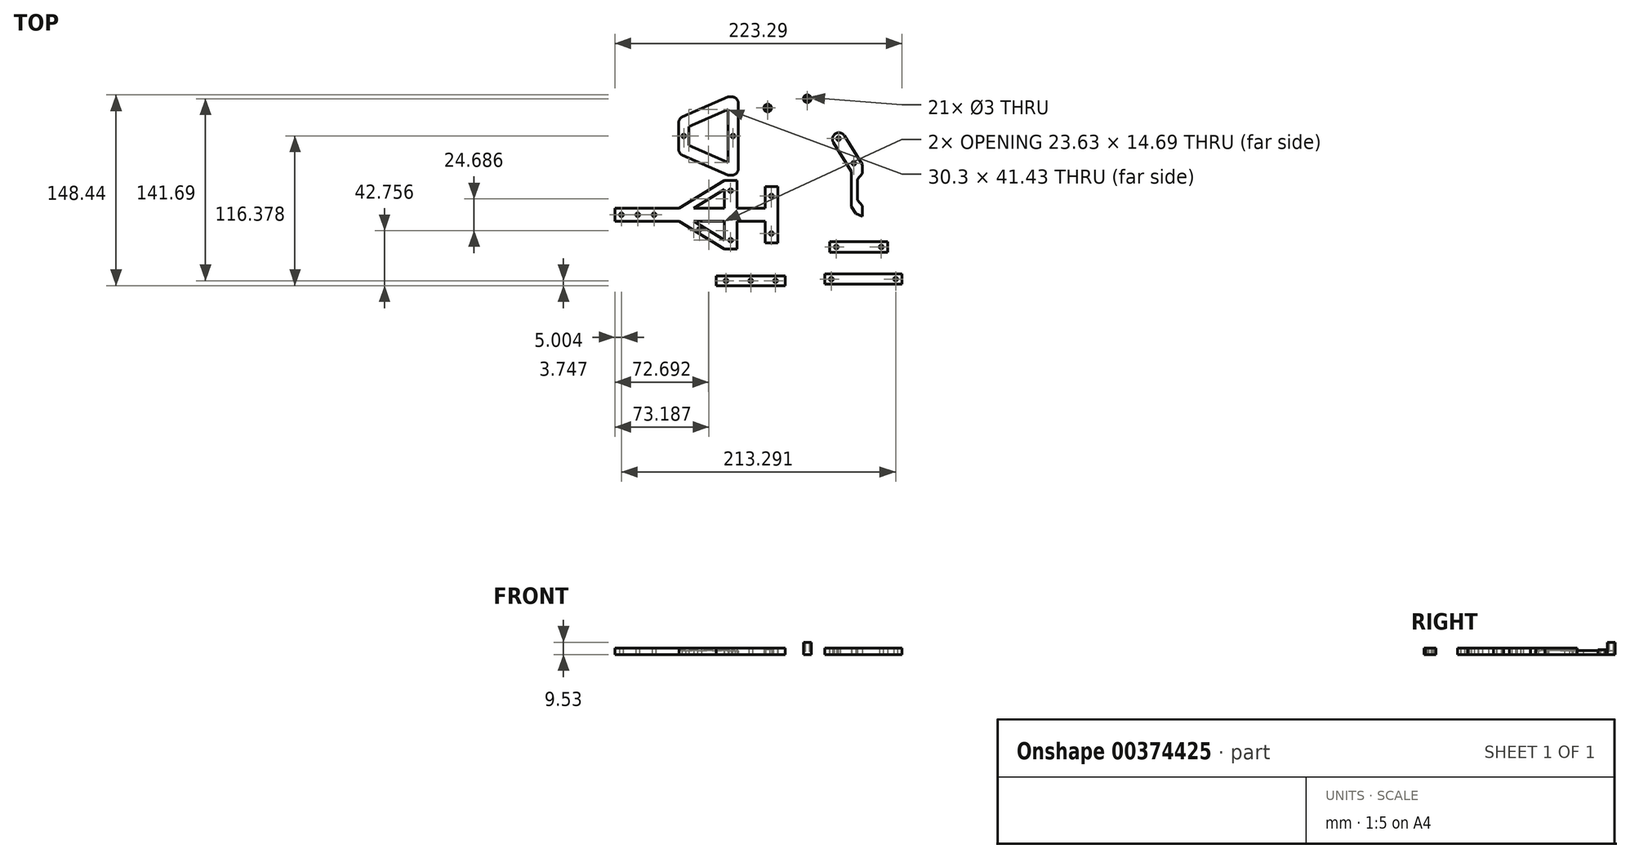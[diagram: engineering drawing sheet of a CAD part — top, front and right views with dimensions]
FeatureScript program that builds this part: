
annotation { "Feature Type Name" : "Feature", "Feature Type Description" : "" }
export const myFeature = defineFeature(function(context is Context, id is Id, definition is map)
    precondition{}
    {
        {
            var Q0;
            Q0=qCreatedBy(makeId("Top.planeOp"),FACE);
            var sketch = newSketch(context, id + "F0", { "sketchPlane" : qUnion([Q0])});
            skLineSegment(sketch, "E0.bottom", {"start": v(-43.53, 84.94) * mm, "end": v(-108.53, 84.94) * mm});
            skLineSegment(sketch, "E0.top", {"start": v(-43.53, 65.26) * mm, "end": v(-108.53, 65.26) * mm});
            skLineSegment(sketch, "E0.left", {"start": v(-43.53, 84.94) * mm, "end": v(-43.53, 65.26) * mm});
            skLineSegment(sketch, "E0.right", {"start": v(-108.53, 84.94) * mm, "end": v(-108.53, 65.26) * mm});
            skPoint(sketch, "E0.middle", {"position": v(-76.03, 75.1) * mm});
            skCircle(sketch, "E1", {"center": v(-96.03, 75.1) * mm, "radius": 1.5 * mm});
            skCircle(sketch, "E2", {"center": v(-57.73, 75.1) * mm, "radius": 1.5 * mm});
            skLineSegment(sketch, "E3.bottom", {"start": v(-49.57, 18.82) * mm, "end": v(-149.57, 18.82) * mm});
            skLineSegment(sketch, "E3.top", {"start": v(-49.57, 8.82) * mm, "end": v(-149.57, 8.82) * mm});
            skLineSegment(sketch, "E3.left", {"start": v(-49.57, 18.82) * mm, "end": v(-49.57, 8.82) * mm});
            skLineSegment(sketch, "E3.right", {"start": v(-149.57, 18.82) * mm, "end": v(-149.57, 8.82) * mm});
            skPoint(sketch, "E3.middle", {"position": v(-99.57, 13.82) * mm});
            skCircle(sketch, "E4", {"center": v(-144.57, 13.82) * mm, "radius": 1.5 * mm});
            skCircle(sketch, "E5", {"center": v(-119.17, 13.82) * mm, "radius": 1.5 * mm});
            skCircle(sketch, "E6", {"center": v(-131.87, 13.82) * mm, "radius": 1.5 * mm});
            skLineSegment(sketch, "E7.bottom", {"start": v(-53.73, 95.81) * mm, "end": v(-61.73, 95.81) * mm});
            skLineSegment(sketch, "E7.top", {"start": v(-53.73, 54.38) * mm, "end": v(-61.73, 54.38) * mm});
            skLineSegment(sketch, "E7.left", {"start": v(-53.73, 95.81) * mm, "end": v(-53.73, 54.38) * mm});
            skLineSegment(sketch, "E7.right", {"start": v(-61.73, 95.81) * mm, "end": v(-61.73, 54.38) * mm});
            skLineSegment(sketch, "E8", {"start": v(-61.73, 95.81) * mm, "end": v(-108.53, 75.1) * mm});
            skLineSegment(sketch, "E9", {"start": v(-108.53, 75.1) * mm, "end": v(-61.73, 54.38) * mm});
            skLineSegment(sketch, "E10", {"start": v(-108.53, 84.94) * mm, "end": v(-61.73, 105.66) * mm});
            skLineSegment(sketch, "E11", {"start": v(-61.73, 105.66) * mm, "end": v(-53.73, 105.66) * mm});
            skLineSegment(sketch, "E12", {"start": v(-53.73, 105.66) * mm, "end": v(-53.73, 95.81) * mm});
            skLineSegment(sketch, "E13", {"start": v(-108.53, 65.26) * mm, "end": v(-61.73, 44.54) * mm});
            skLineSegment(sketch, "E14", {"start": v(-61.73, 44.54) * mm, "end": v(-53.73, 44.54) * mm});
            skLineSegment(sketch, "E15", {"start": v(-53.73, 44.54) * mm, "end": v(-53.73, 54.38) * mm});
            skLineSegment(sketch, "E16", {"start": v(-100.03, 61.5) * mm, "end": v(-100.03, 88.7) * mm});
            skLineSegment(sketch, "E17", {"start": v(-92.03, 57.95) * mm, "end": v(-92.03, 92.24) * mm});
            skCircle(sketch, "E18", {"center": v(-30.8, 96.92) * mm, "radius": 1.5 * mm});
            skCircle(sketch, "E19", {"center": v(-30.8, 96.92) * mm, "radius": 3 * mm});
            skCircle(sketch, "E20", {"center": v(24.35, 73.1) * mm, "radius": 1.5 * mm});
            skLineSegment(sketch, "E21", {"start": v(24.35, 73.1) * mm, "end": v(24.35, 53.98) * mm, "construction": true});
            skLineSegment(sketch, "E22", {"start": v(24.35, 53.98) * mm, "end": v(36.2, 53.98) * mm, "construction": true});
            skLineSegment(sketch, "E23", {"start": v(36.2, 53.98) * mm, "end": v(24.35, 73.1) * mm, "construction": true});
            skCircle(sketch, "E24", {"center": v(36.2, 53.98) * mm, "radius": 1.5 * mm});
            skLineSegment(sketch, "E25", {"start": v(24.35, 73.1) * mm, "end": v(20.1, 70.47) * mm});
            skLineSegment(sketch, "E26", {"start": v(20.1, 70.47) * mm, "end": v(31.95, 51.34) * mm});
            skLineSegment(sketch, "E27", {"start": v(20.1, 70.47) * mm, "end": v(17.73, 74.3) * mm});
            skLineSegment(sketch, "E28", {"start": v(17.73, 74.3) * mm, "end": v(21.98, 76.93) * mm});
            skLineSegment(sketch, "E29", {"start": v(21.98, 76.93) * mm, "end": v(24.35, 73.1) * mm});
            skLineSegment(sketch, "E30", {"start": v(30.27, 63.54) * mm, "end": v(26.02, 60.9) * mm});
            skLineSegment(sketch, "E31.MirrorCS", {"start": v(28.6, 75.74) * mm, "end": v(40.45, 56.6) * mm});
            skLineSegment(sketch, "E32.MirrorCS", {"start": v(28.6, 75.74) * mm, "end": v(26.23, 79.56) * mm});
            skLineSegment(sketch, "E33.MirrorCS", {"start": v(26.23, 79.56) * mm, "end": v(21.98, 76.93) * mm});
            skLineSegment(sketch, "E34.MirrorCS", {"start": v(34.32, 47.52) * mm, "end": v(38.57, 50.15) * mm});
            skLineSegment(sketch, "E35.MirrorCS", {"start": v(42.82, 52.78) * mm, "end": v(38.57, 50.15) * mm});
            skLineSegment(sketch, "E36.MirrorCS", {"start": v(40.45, 56.6) * mm, "end": v(42.82, 52.78) * mm});
            skLineSegment(sketch, "E37", {"start": v(31.95, 51.34) * mm, "end": v(34.32, 47.52) * mm});
            skPoint(sketch, "E38.endSnap0", {"position": v(40.7, 51.47) * mm});
            skLineSegment(sketch, "E39", {"start": v(42.82, 52.78) * mm, "end": v(42.82, 45.78) * mm});
            skLineSegment(sketch, "E40", {"start": v(42.82, 45.78) * mm, "end": v(38.9, 45.78) * mm});
            skLineSegment(sketch, "E41", {"start": v(38.9, 45.78) * mm, "end": v(38.9, 20.78) * mm});
            skLineSegment(sketch, "E42", {"start": v(38.9, 20.78) * mm, "end": v(42.82, 20.78) * mm});
            skLineSegment(sketch, "E43", {"start": v(42.82, 20.78) * mm, "end": v(42.82, 12.66) * mm});
            skLineSegment(sketch, "E44", {"start": v(34.32, 47.52) * mm, "end": v(34.32, 20.16) * mm});
            skLineSegment(sketch, "E45", {"start": v(34.32, 20.16) * mm, "end": v(37.65, 14.77) * mm});
            skLineSegment(sketch, "E46", {"start": v(37.65, 14.77) * mm, "end": v(42.82, 12.66) * mm});
            skLineSegment(sketch, "E47", {"start": v(38.9, 33.28) * mm, "end": v(34.32, 33.28) * mm});
            skPoint(sketch, "E47.endSnap0", {"position": v(34.32, 33.84) * mm});
            skLineSegment(sketch, "E48", {"start": v(42.82, 45.78) * mm, "end": v(38.9, 41.43) * mm});
            skLineSegment(sketch, "E49.MirrorCS", {"start": v(42.82, 20.78) * mm, "end": v(38.9, 25.13) * mm});
            skCircle(sketch, "E50", {"center": v(-63.23, -37.53) * mm, "radius": 1.5 * mm});
            skCircle(sketch, "E51", {"center": v(-24.73, -37.53) * mm, "radius": 1.5 * mm});
            skLineSegment(sketch, "E52", {"start": v(-63.23, -37.53) * mm, "end": v(-24.73, -37.53) * mm});
            skLineSegment(sketch, "E53.bottom", {"start": v(-17.23, -33.78) * mm, "end": v(-70.73, -33.78) * mm});
            skLineSegment(sketch, "E53.top", {"start": v(-17.23, -41.28) * mm, "end": v(-70.73, -41.28) * mm});
            skLineSegment(sketch, "E53.left", {"start": v(-17.23, -33.78) * mm, "end": v(-17.23, -41.28) * mm});
            skLineSegment(sketch, "E53.right", {"start": v(-70.73, -33.78) * mm, "end": v(-70.73, -41.28) * mm});
            skPoint(sketch, "E53.middle", {"position": v(-43.98, -37.53) * mm});
            skPoint(sketch, "E54.centerSnap0", {"position": v(-49.57, 13.82) * mm});
            skCircle(sketch, "E55", {"center": v(-43.98, -37.53) * mm, "radius": 1.5 * mm});
            skCircle(sketch, "E56", {"center": v(-59.57, 32.57) * mm, "radius": 1.5 * mm});
            skLineSegment(sketch, "E57", {"start": v(-59.57, 32.57) * mm, "end": v(-59.57, -5.93) * mm});
            skCircle(sketch, "E58", {"center": v(-59.57, -5.93) * mm, "radius": 1.5 * mm});
            skLineSegment(sketch, "E59.bottom", {"start": v(-54.57, 40.57) * mm, "end": v(-64.57, 40.57) * mm});
            skLineSegment(sketch, "E59.top", {"start": v(-54.57, -12.93) * mm, "end": v(-64.57, -12.93) * mm});
            skLineSegment(sketch, "E59.left", {"start": v(-54.57, 40.57) * mm, "end": v(-54.57, -12.93) * mm});
            skLineSegment(sketch, "E59.right", {"start": v(-64.57, 40.57) * mm, "end": v(-64.57, -12.93) * mm});
            skPoint(sketch, "E59.middle", {"position": v(-59.57, 13.82) * mm});
            skLineSegment(sketch, "E60", {"start": v(-64.57, 40.57) * mm, "end": v(-99.57, 18.82) * mm});
            skLineSegment(sketch, "E61", {"start": v(-88.2, 18.82) * mm, "end": v(-64.57, 33.5) * mm});
            skLineSegment(sketch, "E62", {"start": v(-49.57, 18.82) * mm, "end": v(-27.86, 18.82) * mm});
            skLineSegment(sketch, "E63", {"start": v(-27.86, 18.82) * mm, "end": v(-27.86, 8.82) * mm});
            skLineSegment(sketch, "E64", {"start": v(-27.86, 8.82) * mm, "end": v(-49.57, 8.82) * mm});
            skLineSegment(sketch, "E65.bottom", {"start": v(-22.86, 35.82) * mm, "end": v(-32.86, 35.82) * mm});
            skLineSegment(sketch, "E65.top", {"start": v(-22.86, -8.19) * mm, "end": v(-32.86, -8.19) * mm});
            skLineSegment(sketch, "E65.left", {"start": v(-22.86, 35.82) * mm, "end": v(-22.86, -8.19) * mm});
            skLineSegment(sketch, "E65.right", {"start": v(-32.86, 35.82) * mm, "end": v(-32.86, -8.19) * mm});
            skPoint(sketch, "E65.middle", {"position": v(-27.86, 13.82) * mm});
            skCircle(sketch, "E66", {"center": v(-27.86, 28.42) * mm, "radius": 1.5 * mm});
            skPoint(sketch, "E66.centerSnap0", {"position": v(-27.86, 35.82) * mm});
            skLineSegment(sketch, "E67", {"start": v(-64.57, 13.82) * mm, "end": v(-54.57, 13.82) * mm});
            skCircle(sketch, "E68.MirrorC", {"center": v(-27.86, -0.78) * mm, "radius": 1.5 * mm});
            skCircle(sketch, "E69", {"center": v(0, 104.16) * mm, "radius": 1.5 * mm});
            skCircle(sketch, "E70", {"center": v(0, 104.16) * mm, "radius": 3 * mm});
            skLineSegment(sketch, "E71.bottom", {"start": v(73.72, -32.22) * mm, "end": v(13.72, -32.22) * mm});
            skLineSegment(sketch, "E71.top", {"start": v(73.72, -40.22) * mm, "end": v(13.72, -40.22) * mm});
            skLineSegment(sketch, "E71.left", {"start": v(73.72, -32.22) * mm, "end": v(73.72, -40.22) * mm});
            skLineSegment(sketch, "E71.right", {"start": v(13.72, -32.22) * mm, "end": v(13.72, -40.22) * mm});
            skPoint(sketch, "E71.middle", {"position": v(43.72, -36.22) * mm});
            skLineSegment(sketch, "E72.bottom", {"start": v(62.58, -7.2) * mm, "end": v(17.58, -7.2) * mm});
            skLineSegment(sketch, "E72.top", {"start": v(62.58, -15.2) * mm, "end": v(17.58, -15.2) * mm});
            skLineSegment(sketch, "E72.left", {"start": v(62.58, -7.2) * mm, "end": v(62.58, -15.2) * mm});
            skLineSegment(sketch, "E72.right", {"start": v(17.58, -7.2) * mm, "end": v(17.58, -15.2) * mm});
            skPoint(sketch, "E72.middle", {"position": v(40.08, -11.2) * mm});
            skCircle(sketch, "E73", {"center": v(22.58, -11.2) * mm, "radius": 1.5 * mm});
            skLineSegment(sketch, "E74", {"start": v(40.08, -15.2) * mm, "end": v(40.08, -7.2) * mm});
            skLineSegment(sketch, "E75", {"start": v(43.72, -40.22) * mm, "end": v(43.72, -32.22) * mm});
            skCircle(sketch, "E76.MirrorC", {"center": v(57.58, -11.2) * mm, "radius": 1.5 * mm});
            skCircle(sketch, "E77", {"center": v(18.72, -36.22) * mm, "radius": 1.5 * mm});
            skPoint(sketch, "E77.centerSnap0", {"position": v(13.72, -36.22) * mm});
            skCircle(sketch, "E78.MirrorC", {"center": v(68.72, -36.22) * mm, "radius": 1.5 * mm});
            skPoint(sketch, "E79.endSnap0", {"position": v(-99.57, 8.82) * mm});
            skLineSegment(sketch, "E80", {"start": v(-99.57, 8.82) * mm, "end": v(-64.57, -12.93) * mm});
            skLineSegment(sketch, "E81", {"start": v(-88.2, 8.82) * mm, "end": v(-64.57, -5.87) * mm});
            skLineSegment(sketch, "E82", {"start": v(-85.38, 0) * mm, "end": v(-82.2, 5.1) * mm});
            skCircle(sketch, "E83", {"center": v(-83.8, 2.55) * mm, "radius": 1.5 * mm});
            skSolve(sketch);
        }
        {
            var Q0;
            Q0=makeQuery(id+"F0.imprint","IMPRINT",FACE,{"disambiguationData":[TD([[makeQuery(id+"F0.imprint","IMPRINT",EDGE,{"derivedFrom":sQuery(id+"F0.wireOp",EDGE,"E0.bottom")}),1.0]])]});
            var Q1;
            {var subQ5=sQuery(id+"F0.wireOp",EDGE,"E7.top");Q1=makeQuery(id+"F0.imprint","IMPRINT",FACE,{"disambiguationData":[TD([[makeQuery(id+"F0.imprint","IMPRINT",EDGE,{"derivedFrom":subQ5}),-1.0]])]});}
            var Q2;
            Q2=makeQuery(id+"F0.imprint","IMPRINT",FACE,{"disambiguationData":[TD([[makeQuery(id+"F0.imprint","IMPRINT",EDGE,{"derivedFrom":sQuery(id+"F0.wireOp",EDGE,"E2")}),-1.0]])]});
            var Q3;
            {var subQ4=sQuery(id+"F0.wireOp",EDGE,"E7.top");Q3=makeQuery(id+"F0.imprint","IMPRINT",FACE,{"disambiguationData":[TD([[makeQuery(id+"F0.imprint","IMPRINT",EDGE,{"derivedFrom":subQ4}),1.0]])]});}
            var Q4;
            {var subQ5=sQuery(id+"F0.wireOp",EDGE,"E9");var subQ6=sQuery(id+"F0.wireOp",EDGE,"E0.top");var subQ7=makeQuery(id+"F0.imprint","INTERSECT",VERTEX,{"derivedFrom":[subQ6,subQ5]});Q4=makeQuery(id+"F0.imprint","IMPRINT",FACE,{"disambiguationData":[TD([[makeQuery(id+"F0.imprint","IMPRINT",EDGE,{"disambiguationData":[TD([[subQ7,-1.0]])],"derivedFrom":subQ6}),1.0]])]});}
            var Q5;
            {var subQ0=sQuery(id+"F0.wireOp",EDGE,"E17");var subQ1=sQuery(id+"F0.wireOp",EDGE,"E0.top");var subQ2=makeQuery(id+"F0.imprint","INTERSECT",VERTEX,{"derivedFrom":[subQ1,subQ0]});Q5=makeQuery(id+"F0.imprint","IMPRINT",FACE,{"disambiguationData":[TD([[makeQuery(id+"F0.imprint","IMPRINT",EDGE,{"disambiguationData":[TD([[subQ2,-1.0]])],"derivedFrom":subQ1}),1.0]])]});}
            var Q6;
            {var subQ0=sQuery(id+"F0.wireOp",EDGE,"E9");var subQ1=sQuery(id+"F0.wireOp",EDGE,"E0.top");var subQ2=makeQuery(id+"F0.imprint","INTERSECT",VERTEX,{"derivedFrom":[subQ1,subQ0]});Q6=makeQuery(id+"F0.imprint","IMPRINT",FACE,{"disambiguationData":[TD([[makeQuery(id+"F0.imprint","IMPRINT",EDGE,{"disambiguationData":[TD([[subQ2,-1.0]])],"derivedFrom":subQ1}),-1.0]])]});}
            var Q7;
            Q7=makeQuery(id+"F0.imprint","IMPRINT",FACE,{"disambiguationData":[TD([[makeQuery(id+"F0.imprint","IMPRINT",EDGE,{"derivedFrom":sQuery(id+"F0.wireOp",EDGE,"E1")}),-1.0]])]});
            var Q8;
            {var subQ0=sQuery(id+"F0.wireOp",EDGE,"E17");var subQ1=sQuery(id+"F0.wireOp",EDGE,"E0.top");var subQ2=makeQuery(id+"F0.imprint","INTERSECT",VERTEX,{"derivedFrom":[subQ1,subQ0]});Q8=makeQuery(id+"F0.imprint","IMPRINT",FACE,{"disambiguationData":[TD([[makeQuery(id+"F0.imprint","IMPRINT",EDGE,{"disambiguationData":[TD([[subQ2,-1.0]])],"derivedFrom":subQ1}),-1.0]])]});}
            var Q9;
            {var subQ0=sQuery(id+"F0.wireOp",EDGE,"E17");var subQ1=sQuery(id+"F0.wireOp",EDGE,"E0.bottom");var subQ2=makeQuery(id+"F0.imprint","INTERSECT",VERTEX,{"derivedFrom":[subQ1,subQ0]});Q9=makeQuery(id+"F0.imprint","IMPRINT",FACE,{"disambiguationData":[TD([[makeQuery(id+"F0.imprint","IMPRINT",EDGE,{"disambiguationData":[TD([[subQ2,-1.0]])],"derivedFrom":subQ1}),1.0]])]});}
            var Q10;
            {var subQ0=sQuery(id+"F0.wireOp",EDGE,"E17");var subQ1=sQuery(id+"F0.wireOp",EDGE,"E0.bottom");var subQ2=makeQuery(id+"F0.imprint","INTERSECT",VERTEX,{"derivedFrom":[subQ1,subQ0]});Q10=makeQuery(id+"F0.imprint","IMPRINT",FACE,{"disambiguationData":[TD([[makeQuery(id+"F0.imprint","IMPRINT",EDGE,{"disambiguationData":[TD([[subQ2,-1.0]])],"derivedFrom":subQ1}),-1.0]])]});}
            var Q11;
            {var subQ5=sQuery(id+"F0.wireOp",EDGE,"E7.bottom");Q11=makeQuery(id+"F0.imprint","IMPRINT",FACE,{"disambiguationData":[TD([[makeQuery(id+"F0.imprint","IMPRINT",EDGE,{"derivedFrom":subQ5}),-1.0]])]});}
            var Q12;
            {var subQ5=sQuery(id+"F0.wireOp",EDGE,"E7.bottom");Q12=makeQuery(id+"F0.imprint","IMPRINT",FACE,{"disambiguationData":[TD([[makeQuery(id+"F0.imprint","IMPRINT",EDGE,{"derivedFrom":subQ5}),1.0]])]});}
            extrude(context, id + "F1", {"entities" : qUnion([Q0, Q1, Q2, Q3, Q4, Q5, Q6, Q7, Q8, Q9, Q10, Q11, Q12]), "depth" : 3.18 * mm});
        }
        {
            var Q0;
            Q0=makeQuery(id+"F0.imprint","IMPRINT",FACE,{"disambiguationData":[TD([[makeQuery(id+"F0.imprint","IMPRINT",EDGE,{"derivedFrom":sQuery(id+"F0.wireOp",EDGE,"E18")}),-1.0]])]});
            extrude(context, id + "F2", {"entities" : qUnion([Q0]), "depth" : 3.76 * mm});
        }
        {
            var Q0;
            Q0=makeQuery(id+"F0.imprint","IMPRINT",FACE,{"disambiguationData":[TD([[makeQuery(id+"F0.imprint","IMPRINT",EDGE,{"derivedFrom":sQuery(id+"F0.wireOp",EDGE,"E24")}),-1.0]])]});
            var Q1;
            {var subQ1=sQuery(id+"F0.wireOp",EDGE,"E27");Q1=makeQuery(id+"F0.imprint","IMPRINT",FACE,{"disambiguationData":[TD([[makeQuery(id+"F0.imprint","IMPRINT",EDGE,{"derivedFrom":subQ1}),-1.0]])]});}
            var Q2;
            {var subQ1=sQuery(id+"F0.wireOp",EDGE,"E34.MirrorCS");Q2=makeQuery(id+"F0.imprint","IMPRINT",FACE,{"disambiguationData":[TD([[makeQuery(id+"F0.imprint","IMPRINT",EDGE,{"derivedFrom":subQ1}),-1.0]])]});}
            var Q3;
            {var subQ0=sQuery(id+"F0.wireOp",EDGE,"E40");Q3=makeQuery(id+"F0.imprint","IMPRINT",FACE,{"disambiguationData":[TD([[makeQuery(id+"F0.imprint","IMPRINT",EDGE,{"derivedFrom":subQ0}),1.0]])]});}
            var Q4;
            {var subQ0=sQuery(id+"F0.wireOp",EDGE,"E42");Q4=makeQuery(id+"F0.imprint","IMPRINT",FACE,{"disambiguationData":[TD([[makeQuery(id+"F0.imprint","IMPRINT",EDGE,{"derivedFrom":subQ0}),-1.0]])]});}
            var Q5;
            {var subQ0=sQuery(id+"F0.wireOp",EDGE,"E42");Q5=makeQuery(id+"F0.imprint","IMPRINT",FACE,{"disambiguationData":[TD([[makeQuery(id+"F0.imprint","IMPRINT",EDGE,{"derivedFrom":subQ0}),1.0]])]});}
            var Q6;
            Q6=makeQuery(id+"F0.imprint","IMPRINT",FACE,{"disambiguationData":[TD([[makeQuery(id+"F0.imprint","IMPRINT",EDGE,{"derivedFrom":sQuery(id+"F0.wireOp",EDGE,"E50")}),-1.0]])]});
            var Q7;
            {var subQ0=sQuery(id+"F0.wireOp",EDGE,"E60");Q7=makeQuery(id+"F0.imprint","IMPRINT",FACE,{"disambiguationData":[TD([[makeQuery(id+"F0.imprint","IMPRINT",EDGE,{"derivedFrom":subQ0}),1.0]])]});}
            var Q8;
            Q8=makeQuery(id+"F0.imprint","IMPRINT",FACE,{"disambiguationData":[TD([[makeQuery(id+"F0.imprint","IMPRINT",EDGE,{"derivedFrom":sQuery(id+"F0.wireOp",EDGE,"E56")}),-1.0]])]});
            var Q9;
            {var subQ0=sQuery(id+"F0.wireOp",EDGE,"E57");var subQ1=sQuery(id+"F0.wireOp",EDGE,"E3.bottom");var subQ2=makeQuery(id+"F0.imprint","INTERSECT",VERTEX,{"derivedFrom":[subQ1,subQ0]});Q9=makeQuery(id+"F0.imprint","IMPRINT",FACE,{"disambiguationData":[TD([[makeQuery(id+"F0.imprint","IMPRINT",EDGE,{"disambiguationData":[TD([[subQ2,-1.0]])],"derivedFrom":subQ1}),1.0]])]});}
            var Q10;
            {var subQ0=sQuery(id+"F0.wireOp",EDGE,"E59.left");var subQ1=sQuery(id+"F0.wireOp",EDGE,"E3.bottom");var subQ2=makeQuery(id+"F0.imprint","INTERSECT",VERTEX,{"derivedFrom":[subQ1,subQ0]});Q10=makeQuery(id+"F0.imprint","IMPRINT",FACE,{"disambiguationData":[TD([[makeQuery(id+"F0.imprint","IMPRINT",EDGE,{"disambiguationData":[TD([[subQ2,-1.0]])],"derivedFrom":subQ1}),1.0]])]});}
            var Q11;
            Q11=makeQuery(id+"F0.imprint","IMPRINT",FACE,{"disambiguationData":[TD([[makeQuery(id+"F0.imprint","IMPRINT",EDGE,{"derivedFrom":sQuery(id+"F0.wireOp",EDGE,"E58")}),-1.0]])]});
            var Q12;
            {var subQ0=sQuery(id+"F0.wireOp",EDGE,"mOfxTBTb-6OkJ-vJrD-ISbf-gXZsoh9kn1xD");Q12=makeQuery(id+"F0.imprint","IMPRINT",FACE,{"disambiguationData":[TD([[makeQuery(id+"F0.imprint","IMPRINT",EDGE,{"derivedFrom":subQ0}),1.0]])]});}
            var Q13;
            {var subQ0=sQuery(id+"F0.wireOp",EDGE,"E3.right");Q13=makeQuery(id+"F0.imprint","IMPRINT",FACE,{"disambiguationData":[TD([[makeQuery(id+"F0.imprint","IMPRINT",EDGE,{"derivedFrom":subQ0}),1.0]])]});}
            var Q14;
            {var subQ0=sQuery(id+"F0.wireOp",EDGE,"E59.left");var subQ1=sQuery(id+"F0.wireOp",EDGE,"E3.top");var subQ2=makeQuery(id+"F0.imprint","INTERSECT",VERTEX,{"derivedFrom":[subQ1,subQ0]});Q14=makeQuery(id+"F0.imprint","IMPRINT",FACE,{"disambiguationData":[TD([[makeQuery(id+"F0.imprint","IMPRINT",EDGE,{"disambiguationData":[TD([[subQ2,-1.0]])],"derivedFrom":subQ1}),-1.0]])]});}
            var Q15;
            {var subQ0=sQuery(id+"F0.wireOp",EDGE,"E57");var subQ1=sQuery(id+"F0.wireOp",EDGE,"E3.top");var subQ2=makeQuery(id+"F0.imprint","INTERSECT",VERTEX,{"derivedFrom":[subQ1,subQ0]});Q15=makeQuery(id+"F0.imprint","IMPRINT",FACE,{"disambiguationData":[TD([[makeQuery(id+"F0.imprint","IMPRINT",EDGE,{"disambiguationData":[TD([[subQ2,-1.0]])],"derivedFrom":subQ1}),-1.0]])]});}
            var Q16;
            {var subQ4=sQuery(id+"F0.wireOp",EDGE,"E3.left");Q16=makeQuery(id+"F0.imprint","IMPRINT",FACE,{"disambiguationData":[TD([[makeQuery(id+"F0.imprint","IMPRINT",EDGE,{"derivedFrom":subQ4}),-1.0]])]});}
            var Q17;
            {var subQ0=sQuery(id+"F0.wireOp",EDGE,"E3.left");Q17=makeQuery(id+"F0.imprint","IMPRINT",FACE,{"disambiguationData":[TD([[makeQuery(id+"F0.imprint","IMPRINT",EDGE,{"derivedFrom":subQ0}),1.0]])]});}
            var Q18;
            {var subQ2=sQuery(id+"F0.wireOp",EDGE,"E63");Q18=makeQuery(id+"F0.imprint","IMPRINT",FACE,{"disambiguationData":[TD([[makeQuery(id+"F0.imprint","IMPRINT",EDGE,{"derivedFrom":subQ2}),1.0]])]});}
            var Q19;
            {var subQ0=sQuery(id+"F0.wireOp",EDGE,"E63");Q19=makeQuery(id+"F0.imprint","IMPRINT",FACE,{"disambiguationData":[TD([[makeQuery(id+"F0.imprint","IMPRINT",EDGE,{"derivedFrom":subQ0}),-1.0]])]});}
            var Q20;
            {var subQ0=sQuery(id+"F0.wireOp",EDGE,"E72.right");Q20=makeQuery(id+"F0.imprint","IMPRINT",FACE,{"disambiguationData":[TD([[makeQuery(id+"F0.imprint","IMPRINT",EDGE,{"derivedFrom":subQ0}),1.0]])]});}
            var Q21;
            {var subQ0=sQuery(id+"F0.wireOp",EDGE,"E72.left");Q21=makeQuery(id+"F0.imprint","IMPRINT",FACE,{"disambiguationData":[TD([[makeQuery(id+"F0.imprint","IMPRINT",EDGE,{"derivedFrom":subQ0}),-1.0]])]});}
            var Q22;
            {var subQ1=sQuery(id+"F0.wireOp",EDGE,"E71.left");Q22=makeQuery(id+"F0.imprint","IMPRINT",FACE,{"disambiguationData":[TD([[makeQuery(id+"F0.imprint","IMPRINT",EDGE,{"derivedFrom":subQ1}),-1.0]])]});}
            var Q23;
            {var subQ1=sQuery(id+"F0.wireOp",EDGE,"E71.right");Q23=makeQuery(id+"F0.imprint","IMPRINT",FACE,{"disambiguationData":[TD([[makeQuery(id+"F0.imprint","IMPRINT",EDGE,{"derivedFrom":subQ1}),1.0]])]});}
            var Q24;
            {var subQ1=sQuery(id+"F0.wireOp",EDGE,"xufnJeBo-MPzs-RzrS-7tlF-2dog0HHq910d");Q24=makeQuery(id+"F0.imprint","IMPRINT",FACE,{"disambiguationData":[TD([[makeQuery(id+"F0.imprint","IMPRINT",EDGE,{"derivedFrom":subQ1}),1.0]])]});}
            var Q25;
            {var subQ0=sQuery(id+"F0.wireOp",EDGE,"7ee9f3b0-d933-47a8-aa5e-a2f9af07bda80.MirrorCS");Q25=makeQuery(id+"F0.imprint","IMPRINT",FACE,{"disambiguationData":[TD([[makeQuery(id+"F0.imprint","IMPRINT",EDGE,{"derivedFrom":subQ0}),-1.0]])]});}
            var Q26;
            {var subQ4=sQuery(id+"F0.wireOp",EDGE,"7OHdfdEe-NtJ8-Z7NY-3w09-MJT2khb5SlhV");Q26=makeQuery(id+"F0.imprint","IMPRINT",FACE,{"disambiguationData":[TD([[makeQuery(id+"F0.imprint","IMPRINT",EDGE,{"derivedFrom":subQ4}),1.0]])]});}
            var Q27;
            {var subQ3=sQuery(id+"F0.wireOp",EDGE,"g9AG0mZW-TdXm-As67-mIht-S1R7DHisCtON");var subQ5=sQuery(id+"F0.wireOp",EDGE,"7DuqVu71-Rhnx-5vvU-Qr0l-788eBSlq6G7L");var subQ6=makeQuery(id+"F0.imprint","INTERSECT",VERTEX,{"disambiguationData":[OD(0.0)],"derivedFrom":[subQ5,subQ3]});Q27=makeQuery(id+"F0.imprint","IMPRINT",FACE,{"disambiguationData":[TD([[makeQuery(id+"F0.imprint","IMPRINT",EDGE,{"disambiguationData":[TD([[subQ6,-1.0]])],"derivedFrom":subQ5}),-1.0]])]});}
            var Q28;
            {var subQ0=sQuery(id+"F0.wireOp",EDGE,"ChTrYIKO-wZwi-auNg-qPgf-PBuc1KXKA6jE");var subQ5=sQuery(id+"F0.wireOp",EDGE,"E3.top");var subQ7=makeQuery(id+"F0.imprint","INTERSECT",VERTEX,{"derivedFrom":[subQ5,subQ0]});Q28=makeQuery(id+"F0.imprint","IMPRINT",FACE,{"disambiguationData":[TD([[makeQuery(id+"F0.imprint","IMPRINT",EDGE,{"disambiguationData":[TD([[subQ7,1.0]])],"derivedFrom":subQ5}),-1.0]])]});}
            var Q29;
            {var subQ2=sQuery(id+"F0.wireOp",EDGE,"E3.bottom");var subQ9=makeQuery(id+"F0.imprint","INTERSECT",VERTEX,{"derivedFrom":[subQ2,sQuery(id+"F0.wireOp",EDGE,"E61")]});Q29=makeQuery(id+"F0.imprint","IMPRINT",FACE,{"disambiguationData":[TD([[makeQuery(id+"F0.imprint","IMPRINT",EDGE,{"disambiguationData":[TD([[subQ9,1.0]])],"derivedFrom":subQ2}),1.0]])]});}
            var Q30;
            {var subQ0=sQuery(id+"F0.wireOp",EDGE,"ChTrYIKO-wZwi-auNg-qPgf-PBuc1KXKA6jE");var subQ1=sQuery(id+"F0.wireOp",EDGE,"E3.top");var subQ2=makeQuery(id+"F0.imprint","INTERSECT",VERTEX,{"derivedFrom":[subQ1,subQ0]});Q30=makeQuery(id+"F0.imprint","IMPRINT",FACE,{"disambiguationData":[TD([[makeQuery(id+"F0.imprint","IMPRINT",EDGE,{"disambiguationData":[TD([[subQ2,1.0]])],"derivedFrom":subQ1}),1.0]])]});}
            var Q31;
            {var subQ8=sQuery(id+"F0.wireOp",EDGE,"eCOabPo4-bhrj-6nFi-8yjy-s5uLOmIM5T1K");Q31=makeQuery(id+"F0.imprint","IMPRINT",FACE,{"disambiguationData":[TD([[makeQuery(id+"F0.imprint","IMPRINT",EDGE,{"derivedFrom":subQ8}),1.0]])]});}
            var Q32;
            {var subQ1=sQuery(id+"F0.wireOp",EDGE,"E80");var subQ6=sQuery(id+"F0.wireOp",EDGE,"E3.top");var subQ9=makeQuery(id+"F0.imprint","INTERSECT",VERTEX,{"derivedFrom":[subQ6,subQ1]});Q32=makeQuery(id+"F0.imprint","IMPRINT",FACE,{"disambiguationData":[TD([[makeQuery(id+"F0.imprint","IMPRINT",EDGE,{"disambiguationData":[TD([[subQ9,1.0]])],"derivedFrom":subQ6}),1.0]])]});}
            var Q33;
            {var subQ5=sQuery(id+"F0.wireOp",EDGE,"E81");var subQ6=sQuery(id+"F0.wireOp",EDGE,"E59.right");var subQ7=makeQuery(id+"F0.imprint","INTERSECT",VERTEX,{"derivedFrom":[subQ6,subQ5]});Q33=makeQuery(id+"F0.imprint","IMPRINT",FACE,{"disambiguationData":[TD([[makeQuery(id+"F0.imprint","IMPRINT",EDGE,{"disambiguationData":[TD([[subQ7,1.0]])],"derivedFrom":subQ5}),-1.0]])]});}
            extrude(context, id + "F3", {"entities" : qUnion([Q0, Q1, Q2, Q3, Q4, Q5, Q6, Q7, Q8, Q9, Q10, Q11, Q12, Q13, Q14, Q15, Q16, Q17, Q18, Q19, Q20, Q21, Q22, Q23, Q24, Q25, Q26, Q27, Q28, Q29, Q30, Q31, Q32, Q33]), "depth" : 5.08 * mm});
        }
        {
            var Q0;
            Q0=makeQuery(id+"F3.opExtrude","SWEPT_EDGE",EDGE,{"disambiguationData":[OSD([sQuery(id+"F0.wireOp",EDGE,"E27"),sQuery(id+"F0.wireOp",EDGE,"E28")])]});
            var Q1;
            Q1=makeQuery(id+"F3.opExtrude","SWEPT_EDGE",EDGE,{"disambiguationData":[OSD([sQuery(id+"F0.wireOp",EDGE,"E32.MirrorCS"),sQuery(id+"F0.wireOp",EDGE,"E33.MirrorCS")])]});
            fillet(context, id + "F4", {"entities" : qUnion([Q0, Q1]), "radius" : 5 * mm, "tangentPropagation" : true, "allowEdgeOverflow" : false});
        }
        {
            var Q0;
            Q0=makeQuery(id+"F0.imprint","IMPRINT",FACE,{"disambiguationData":[TD([[makeQuery(id+"F0.imprint","IMPRINT",EDGE,{"derivedFrom":sQuery(id+"F0.wireOp",EDGE,"E69")}),-1.0]])]});
            extrude(context, id + "F5", {"entities" : qUnion([Q0]), "depth" : 9.53 * mm});
        }
        {
            var Q0;
            Q0=makeQuery(id+"F1.opExtrude","SWEPT_EDGE",EDGE,{"disambiguationData":[OSD([sQuery(id+"F0.wireOp",EDGE,"E13"),sQuery(id+"F0.wireOp",EDGE,"E16")])]});
            var Q1;
            Q1=makeQuery(id+"F1.opExtrude","SWEPT_EDGE",EDGE,{"disambiguationData":[OSD([sQuery(id+"F0.wireOp",EDGE,"E10"),sQuery(id+"F0.wireOp",EDGE,"E16")])]});
            var Q2;
            Q2=makeQuery(id+"F1.opExtrude","SWEPT_EDGE",EDGE,{"disambiguationData":[OSD([sQuery(id+"F0.wireOp",EDGE,"E11"),sQuery(id+"F0.wireOp",EDGE,"E12")])]});
            var Q3;
            Q3=makeQuery(id+"F1.opExtrude","SWEPT_EDGE",EDGE,{"disambiguationData":[OSD([sQuery(id+"F0.wireOp",EDGE,"E14"),sQuery(id+"F0.wireOp",EDGE,"E15")])]});
            fillet(context, id + "F6", {"entities" : qUnion([Q0, Q1, Q2, Q3]), "radius" : 5 * mm, "tangentPropagation" : true, "allowEdgeOverflow" : false});
        }
    });
